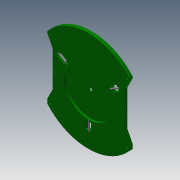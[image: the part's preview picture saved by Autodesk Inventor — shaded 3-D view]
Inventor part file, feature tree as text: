
AUTODESK INVENTOR PART (.ipt)
format: ipt  version: 2013 (Build 170138000, 138)  size: 548,352 bytes
history: native  units: mm
features: extrude x21, sketch x21
ambient origin geometry x8: Origin, YZ Plane, XZ Plane, XY Plane, X Axis, Y Axis, Z Axis, Center Point
bodies: Solid1 (feature_tree)
feature tree (42):
  extrude  "Extrusion1"  Depth=4.0mm
  extrude  "Extrusion2"  Depth=4.0mm
  extrude  "Extrusion3"  Depth=4.0mm
  extrude  "Extrusion4"  Depth=4.0mm
  extrude  "Extrusion5"  Depth=4.0mm
  extrude  "Extrusion6"  Depth=4.0mm
  extrude  "Extrusion7"  Depth=4.0mm
  sketch  "Sketch8"  dims[d14=4.0mm d15=4.0mm]
  sketch  "Sketch9"  dims[d16=4.0mm d17=4.0mm]
  sketch  "Sketch10"  dims[d18=4.0mm d19=4.0mm]
  extrude  "Extrusion8"  Depth=4.0mm
  extrude  "Extrusion9"  Depth=4.0mm
  extrude  "Extrusion10"  Depth=4.0mm
  extrude  "Extrusion11"  Depth=4.0mm
  extrude  "Extrusion12"  Depth=4.0mm
  extrude  "Extrusion13"  Depth=2.0mm TaperAngle=0.0deg
  extrude  "Extrusion14"  Depth=8.0mm TaperAngle=0.0deg
  extrude  "Extrusion15"  Depth=10.0mm TaperAngle=0.0deg
  extrude  "Extrusion16"  Depth=8.0mm
  sketch  "Sketch18"  dims[d41=11.3mm d42=0.0mm d43=11.3mm d44=0.0mm]
  extrude  "Extrusion17"  Depth=11.3mm TaperAngle=0.0deg
  extrude  "Extrusion18"  Depth=11.3mm TaperAngle=0.0deg
  extrude  "Extrusion19"  Depth=100.0mm
  extrude  "Extrusion20"  Depth=6.0mm
  extrude  "Extrusion21"  Depth=3.0mm
  sketch  "Sketch1"  dims[d0=4.0mm d1=4.0mm]
  sketch  "Sketch2"  dims[d2=4.0mm d3=4.0mm]
  sketch  "Sketch3"  dims[d4=4.0mm d5=4.0mm]
  sketch  "Sketch4"  dims[d6=4.0mm d7=4.0mm]
  sketch  "Sketch5"  dims[d8=4.0mm d9=4.0mm]
  sketch  "Sketch6"  dims[d10=4.0mm d11=4.0mm]
  sketch  "Sketch7"  dims[d12=4.0mm d13=4.0mm]
  sketch  "Sketch11"  dims[d20=4.0mm d21=4.0mm]
  sketch  "Sketch12"  dims[d22=4.0mm d23=4.0mm]
  sketch  "Sketch13"  dims[d24=4.0mm d25=2.0mm d26=0.0mm]
  sketch  "Sketch14"  dims[d27=1.3mm d28=0.0mm d29=8.0mm d30=0.0mm]
  sketch  "Sketch15"  dims[d31=10.0mm d32=0.0mm d33=10.0mm d34=0.0mm]
  sketch  "Sketch16"  dims[d35=3.0mm d36=8.0mm]
  sketch  "Sketch17"  dims[d37=11.3mm d38=0.0mm d39=11.3mm d40=0.0mm]
  sketch  "Sketch19"  dims[d45=100.0mm d46=100.0mm]
  sketch  "Sketch20"  dims[d47=11.3mm d48=0.0mm d49=6.0mm]
  sketch  "Sketch21"  dims[d50=11.3mm d51=0.0mm d52=3.0mm d53=3.0mm d54=11.3mm d55=0.0mm d56=11.3mm d57=0.0mm d58=1.3mm d59=0.0mm d60=120.0mm d63=60.191mm d65=37.2mm d66=14.209mm d67=91.5mm d68=8.0mm d69=0.0mm d70=3.8mm d71=0.0mm d72=10.0mm d73=20.0mm d74=10.0mm d75=14.0mm d87=20.0mm d88=10.0mm d89=20.0mm d90=10.0mm d91=14.0mm d92=10.0mm d93=14.0mm d94=10.0mm d95=10.0mm d96=0.0mm d97=30.0deg d98=2.5mm d99=2.5mm d100=2.5mm d101=2.5mm d102=2.5mm d103=2.5mm d104=2.5mm d105=0.0mm d106=20.0mm d107=0.0mm d108=20.0mm d109=0.0mm d110=20.0mm d111=0.0mm]
